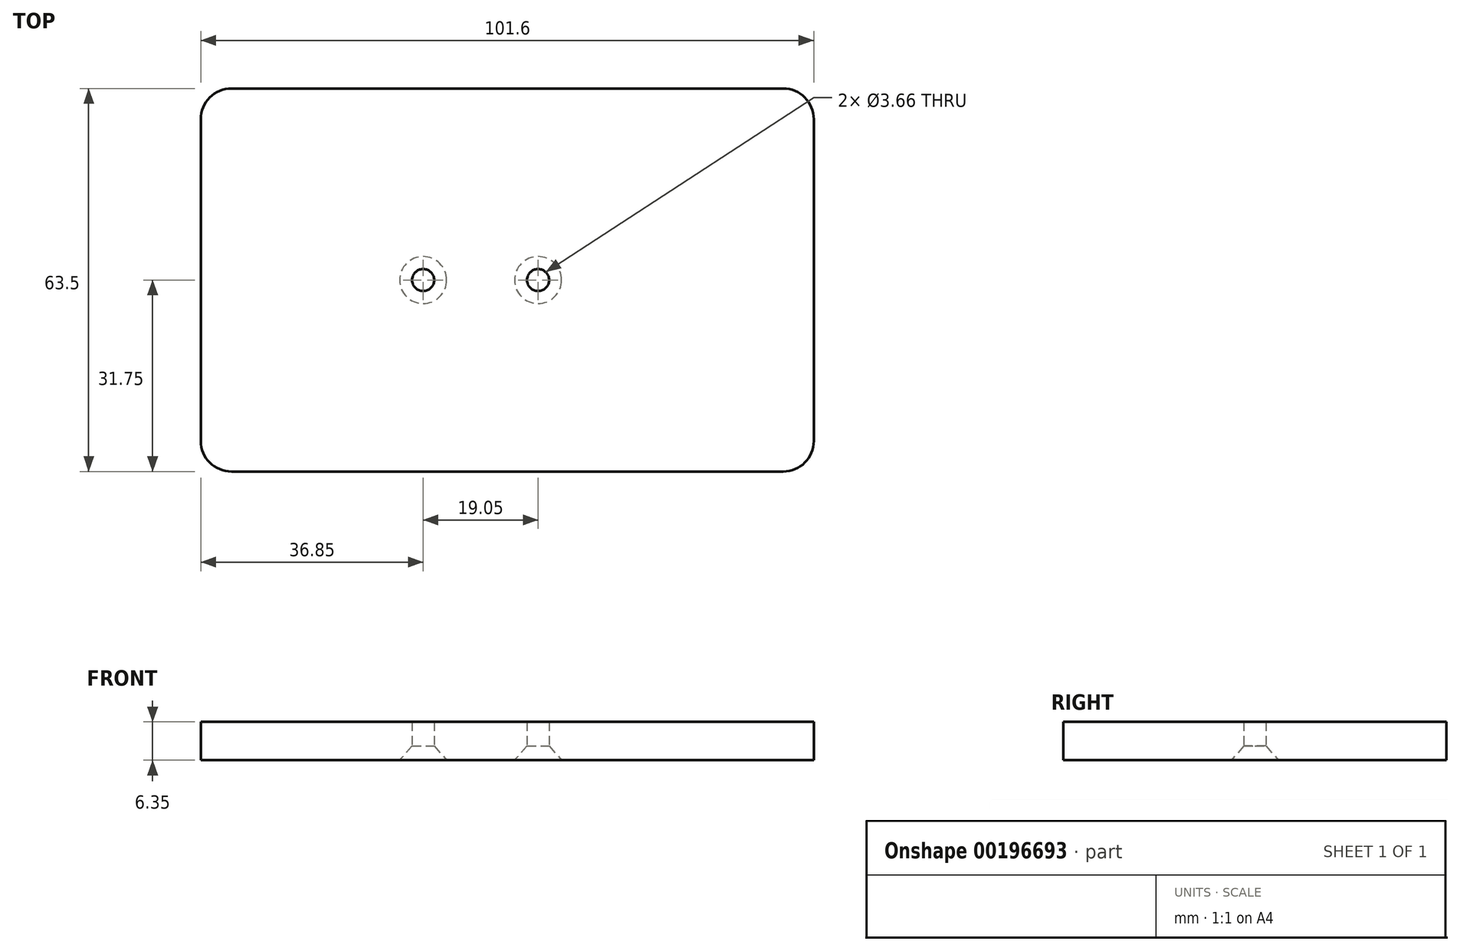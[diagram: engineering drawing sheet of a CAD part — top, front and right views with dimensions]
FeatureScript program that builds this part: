
annotation { "Feature Type Name" : "Feature", "Feature Type Description" : "" }
export const myFeature = defineFeature(function(context is Context, id is Id, definition is map)
    precondition{}
    {
        {
            var Q0;
            Q0=qCreatedBy(makeId("Top.planeOp"),FACE);
            var sketch = newSketch(context, id + "F0", { "sketchPlane" : qUnion([Q0])});
            skLineSegment(sketch, "E0.bottom", {"start": v(-50.8, 31.75) * mm, "end": v(50.8, 31.75) * mm});
            skLineSegment(sketch, "E0.top", {"start": v(-50.8, -31.75) * mm, "end": v(50.8, -31.75) * mm});
            skLineSegment(sketch, "E0.left", {"start": v(-50.8, 31.75) * mm, "end": v(-50.8, -31.75) * mm});
            skLineSegment(sketch, "E0.right", {"start": v(50.8, 31.75) * mm, "end": v(50.8, -31.75) * mm});
            skPoint(sketch, "E0.middle", {"position": v(0, 0) * mm});
            skPoint(sketch, "E1", {"position": v(-13.95, 0) * mm});
            skPoint(sketch, "E2", {"position": v(5.1, 0) * mm});
            skSolve(sketch);
        }
        {
            var Q0;
            Q0 = qSketchRegion(id + "F0", true);
            extrude(context, id + "F1", {"entities" : qUnion([Q0]), "depth" : 6.35 * mm});
        }
        {
            var Q0;
            Q0=sQuery(id+"F0.wireOp",VERTEX,"E1");
            var Q1;
            Q1=sQuery(id+"F0.wireOp",VERTEX,"E2");
            var Q2;
            Q2=makeQuery(id+"F1.opExtrude","SWEPT_BODY",BODY,{"disambiguationData":[OSD([sQuery(id+"F0.wireOp",EDGE,"E0.bottom"),sQuery(id+"F0.wireOp",EDGE,"E0.top"),sQuery(id+"F0.wireOp",EDGE,"E0.left"),sQuery(id+"F0.wireOp",EDGE,"E0.right")])]});
            hole(context, id + "F2", {"style" : HoleStyle.C_SINK, "endStyle" : HoleEndStyle.THROUGH, "oppositeDirection" : true, "standardTappedOrClearance" : lookupTablePath({ "standard" : "ANSI", "fit" : "Close", "size" : "#6", "type" : "Clearance" }), "standardBlindInLast" : lookupTablePath({ "fit" : "Close", "standard" : "ANSI", "size" : "#6", "type" : "Clearance" }), "holeDiameter" : 3.66 * mm, "cSinkDiameter" : 7.8 * mm, "cSinkAngle" : 82 * degree, "locations" : qUnion([Q0, Q1]), "scope" : qUnion([Q2]), "tappedDepth" : 12.7 * mm, "tapClearance" : 3});
        }
        {
            var Q0;
            Q0=makeQuery(id+"F1.opExtrude","SWEPT_EDGE",EDGE,{"disambiguationData":[OSD([sQuery(id+"F0.wireOp",EDGE,"E0.top"),sQuery(id+"F0.wireOp",EDGE,"E0.left")])]});
            var Q1;
            Q1=makeQuery(id+"F1.opExtrude","SWEPT_EDGE",EDGE,{"disambiguationData":[OSD([sQuery(id+"F0.wireOp",EDGE,"E0.bottom"),sQuery(id+"F0.wireOp",EDGE,"E0.left")])]});
            var Q2;
            Q2=makeQuery(id+"F1.opExtrude","SWEPT_EDGE",EDGE,{"disambiguationData":[OSD([sQuery(id+"F0.wireOp",EDGE,"E0.top"),sQuery(id+"F0.wireOp",EDGE,"E0.right")])]});
            var Q3;
            Q3=makeQuery(id+"F1.opExtrude","SWEPT_EDGE",EDGE,{"disambiguationData":[OSD([sQuery(id+"F0.wireOp",EDGE,"E0.bottom"),sQuery(id+"F0.wireOp",EDGE,"E0.right")])]});
            fillet(context, id + "F3", {"entities" : qUnion([Q0, Q1, Q2, Q3]), "radius" : 5.08 * mm, "tangentPropagation" : true, "allowEdgeOverflow" : false});
        }
    });
